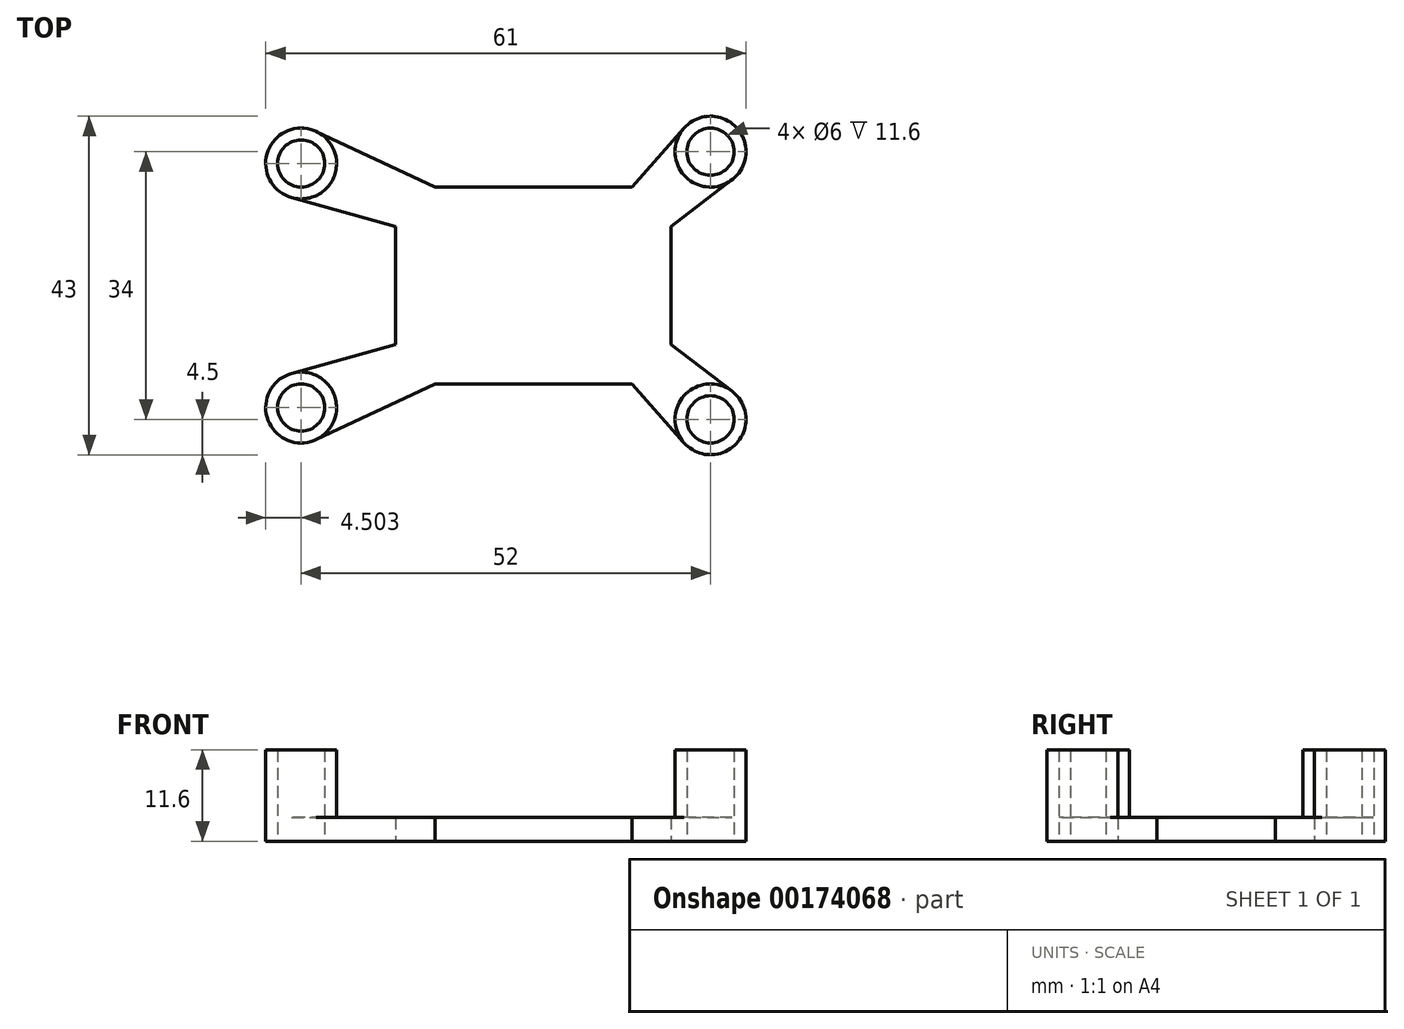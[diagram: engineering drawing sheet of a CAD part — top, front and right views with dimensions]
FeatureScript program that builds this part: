
annotation { "Feature Type Name" : "Feature", "Feature Type Description" : "" }
export const myFeature = defineFeature(function(context is Context, id is Id, definition is map)
    precondition{}
    {
        {
            var Q0;
            Q0=qCreatedBy(makeId("Top.planeOp"),FACE);
            var sketch = newSketch(context, id + "F0", { "sketchPlane" : qUnion([Q0])});
            skCircle(sketch, "E0", {"center": v(-27.4, 15.5) * mm, "radius": 4.5 * mm});
            skCircle(sketch, "E1", {"center": v(-27.4, -15.5) * mm, "radius": 4.5 * mm});
            skCircle(sketch, "E2", {"center": v(24.6, 17) * mm, "radius": 4.5 * mm});
            skCircle(sketch, "E3", {"center": v(24.6, -17) * mm, "radius": 4.5 * mm});
            skLineSegment(sketch, "E4.bottom", {"start": v(-15.4, 12.5) * mm, "end": v(19.6, 12.5) * mm});
            skLineSegment(sketch, "E4.top", {"start": v(-15.4, -12.5) * mm, "end": v(19.6, -12.5) * mm});
            skLineSegment(sketch, "E4.left", {"start": v(-15.4, 12.5) * mm, "end": v(-15.4, -12.5) * mm});
            skLineSegment(sketch, "E4.right", {"start": v(19.6, 12.5) * mm, "end": v(19.6, -12.5) * mm});
            skCircle(sketch, "E5", {"center": v(-27.4, 15.5) * mm, "radius": 3 * mm});
            skCircle(sketch, "E6", {"center": v(-27.4, -15.5) * mm, "radius": 3 * mm});
            skCircle(sketch, "E7", {"center": v(24.6, 17) * mm, "radius": 3 * mm});
            skCircle(sketch, "E8", {"center": v(24.6, -17) * mm, "radius": 3 * mm});
            skLineSegment(sketch, "E9", {"start": v(-10.4, 12.5) * mm, "end": v(-25.5, 19.57) * mm});
            skLineSegment(sketch, "E10", {"start": v(-15.4, 7.5) * mm, "end": v(-28.6, 11.16) * mm});
            skLineSegment(sketch, "E11", {"start": v(-15.4, -7.5) * mm, "end": v(-28.6, -11.16) * mm});
            skLineSegment(sketch, "E12", {"start": v(-10.4, -12.5) * mm, "end": v(-25.5, -19.57) * mm});
            skLineSegment(sketch, "E13", {"start": v(14.6, -12.5) * mm, "end": v(21.23, -19.98) * mm});
            skLineSegment(sketch, "E14", {"start": v(19.6, -7.5) * mm, "end": v(27.33, -13.43) * mm});
            skLineSegment(sketch, "E15", {"start": v(19.6, 7.5) * mm, "end": v(27.33, 13.43) * mm});
            skLineSegment(sketch, "E16", {"start": v(14.6, 12.5) * mm, "end": v(21.23, 19.98) * mm});
            skSolve(sketch);
        }
        {
            var Q0;
            {var subQ0=sQuery(id+"F0.wireOp",EDGE,"E11");Q0=makeQuery(id+"F0.imprint","IMPRINT",FACE,{"disambiguationData":[TD([[makeQuery(id+"F0.imprint","IMPRINT",EDGE,{"derivedFrom":subQ0}),1.0]])]});}
            var Q1;
            {var subQ0=sQuery(id+"F0.wireOp",EDGE,"E4.left");var subQ3=sQuery(id+"F0.wireOp",EDGE,"E4.bottom");var subQ4=makeQuery(id+"F0.imprint","INTERSECT",VERTEX,{"derivedFrom":[subQ3,subQ0]});Q1=makeQuery(id+"F0.imprint","IMPRINT",FACE,{"disambiguationData":[TD([[makeQuery(id+"F0.imprint","IMPRINT",EDGE,{"disambiguationData":[TD([[subQ4,-1.0]])],"derivedFrom":subQ3}),-1.0]])]});}
            var Q2;
            {var subQ4=sQuery(id+"F0.wireOp",EDGE,"E9");Q2=makeQuery(id+"F0.imprint","IMPRINT",FACE,{"disambiguationData":[TD([[makeQuery(id+"F0.imprint","IMPRINT",EDGE,{"derivedFrom":subQ4}),1.0]])]});}
            var Q3;
            {var subQ0=sQuery(id+"F0.wireOp",EDGE,"E13");Q3=makeQuery(id+"F0.imprint","IMPRINT",FACE,{"disambiguationData":[TD([[makeQuery(id+"F0.imprint","IMPRINT",EDGE,{"derivedFrom":subQ0}),1.0]])]});}
            var Q4;
            {var subQ0=sQuery(id+"F0.wireOp",EDGE,"E15");Q4=makeQuery(id+"F0.imprint","IMPRINT",FACE,{"disambiguationData":[TD([[makeQuery(id+"F0.imprint","IMPRINT",EDGE,{"derivedFrom":subQ0}),1.0]])]});}
            extrude(context, id + "F1", {"entities" : qUnion([Q0, Q1, Q2, Q3, Q4]), "depth" : 3 * mm});
        }
        {
            var Q0;
            Q0=makeQuery(id+"F0.imprint","IMPRINT",FACE,{"disambiguationData":[TD([[makeQuery(id+"F0.imprint","IMPRINT",EDGE,{"derivedFrom":sQuery(id+"F0.wireOp",EDGE,"E6")}),-1.0]])]});
            var Q1;
            Q1=makeQuery(id+"F0.imprint","IMPRINT",FACE,{"disambiguationData":[TD([[makeQuery(id+"F0.imprint","IMPRINT",EDGE,{"derivedFrom":sQuery(id+"F0.wireOp",EDGE,"E8")}),-1.0]])]});
            var Q2;
            Q2=makeQuery(id+"F0.imprint","IMPRINT",FACE,{"disambiguationData":[TD([[makeQuery(id+"F0.imprint","IMPRINT",EDGE,{"derivedFrom":sQuery(id+"F0.wireOp",EDGE,"E7")}),-1.0]])]});
            var Q3;
            Q3=makeQuery(id+"F0.imprint","IMPRINT",FACE,{"disambiguationData":[TD([[makeQuery(id+"F0.imprint","IMPRINT",EDGE,{"derivedFrom":sQuery(id+"F0.wireOp",EDGE,"E5")}),-1.0]])]});
            extrude(context, id + "F2", {"entities" : qUnion([Q0, Q1, Q2, Q3]), "operationType" : NewBodyOperationType.ADD, "depth" : 11.6 * mm});
        }
    });
